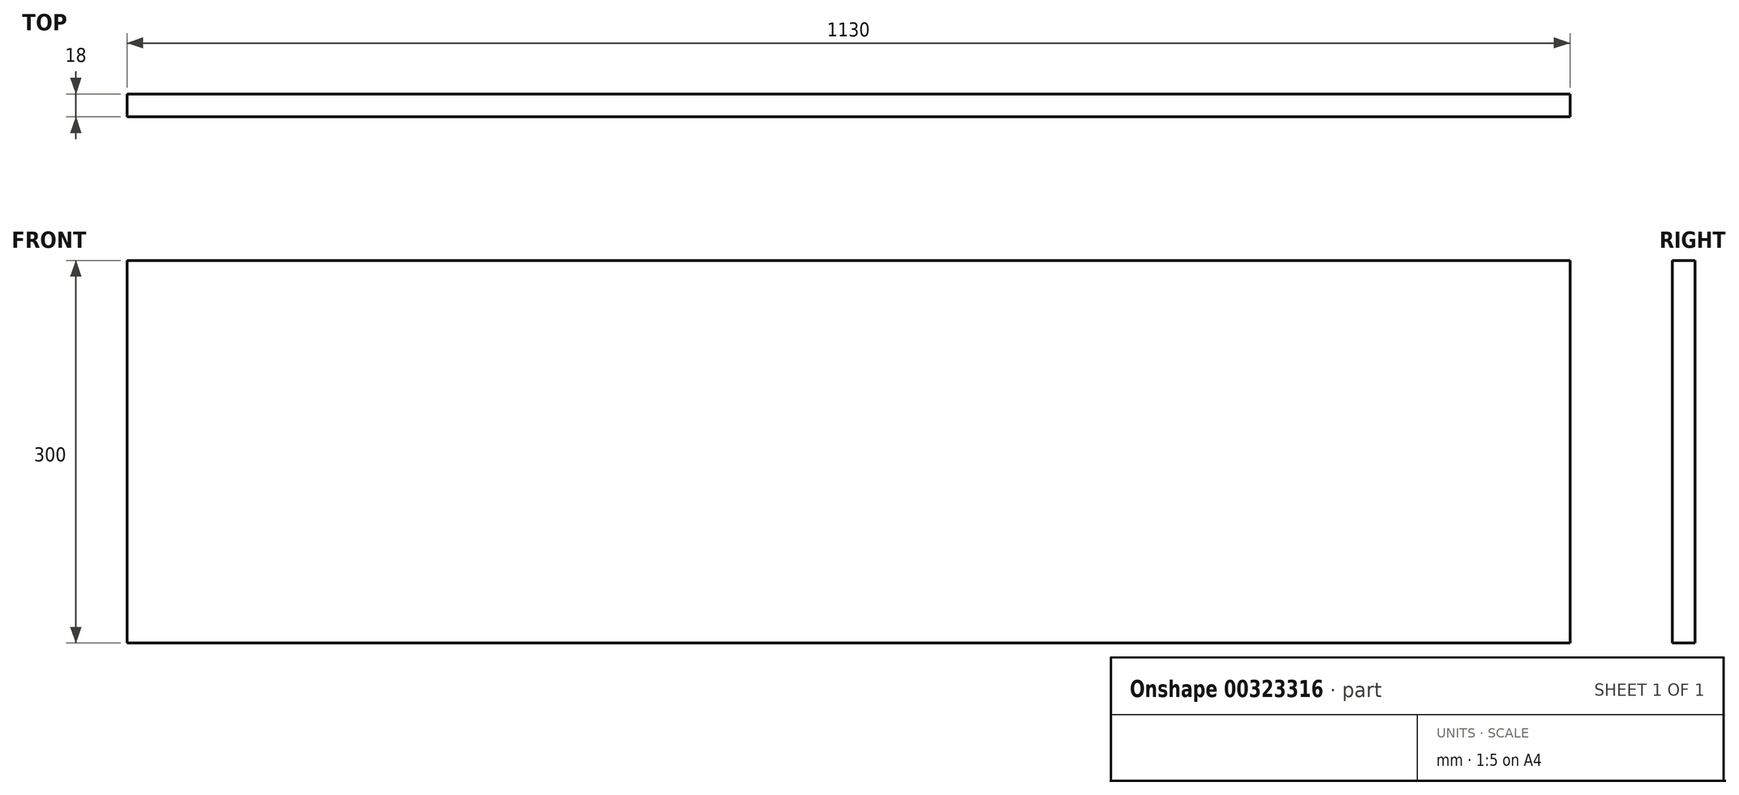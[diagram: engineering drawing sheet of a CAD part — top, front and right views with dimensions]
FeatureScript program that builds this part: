
annotation { "Feature Type Name" : "Feature", "Feature Type Description" : "" }
export const myFeature = defineFeature(function(context is Context, id is Id, definition is map)
    precondition{}
    {
        {
            var Q0;
            Q0=qCreatedBy(makeId("Front.planeOp"),FACE);
            var sketch = newSketch(context, id + "F0", { "sketchPlane" : qUnion([Q0])});
            skLineSegment(sketch, "E0.bottom", {"start": v(0, 0) * mm, "end": v(1130, 0) * mm});
            skLineSegment(sketch, "E0.top", {"start": v(0, 300) * mm, "end": v(1130, 300) * mm});
            skLineSegment(sketch, "E0.left", {"start": v(0, 0) * mm, "end": v(0, 300) * mm});
            skLineSegment(sketch, "E0.right", {"start": v(1130, 0) * mm, "end": v(1130, 300) * mm});
            skSolve(sketch);
        }
        {
            var Q0;
            Q0 = qSketchRegion(id + "F0", true);
            extrude(context, id + "F1", {"entities" : qUnion([Q0]), "depth" : 18 * mm});
        }
    });
